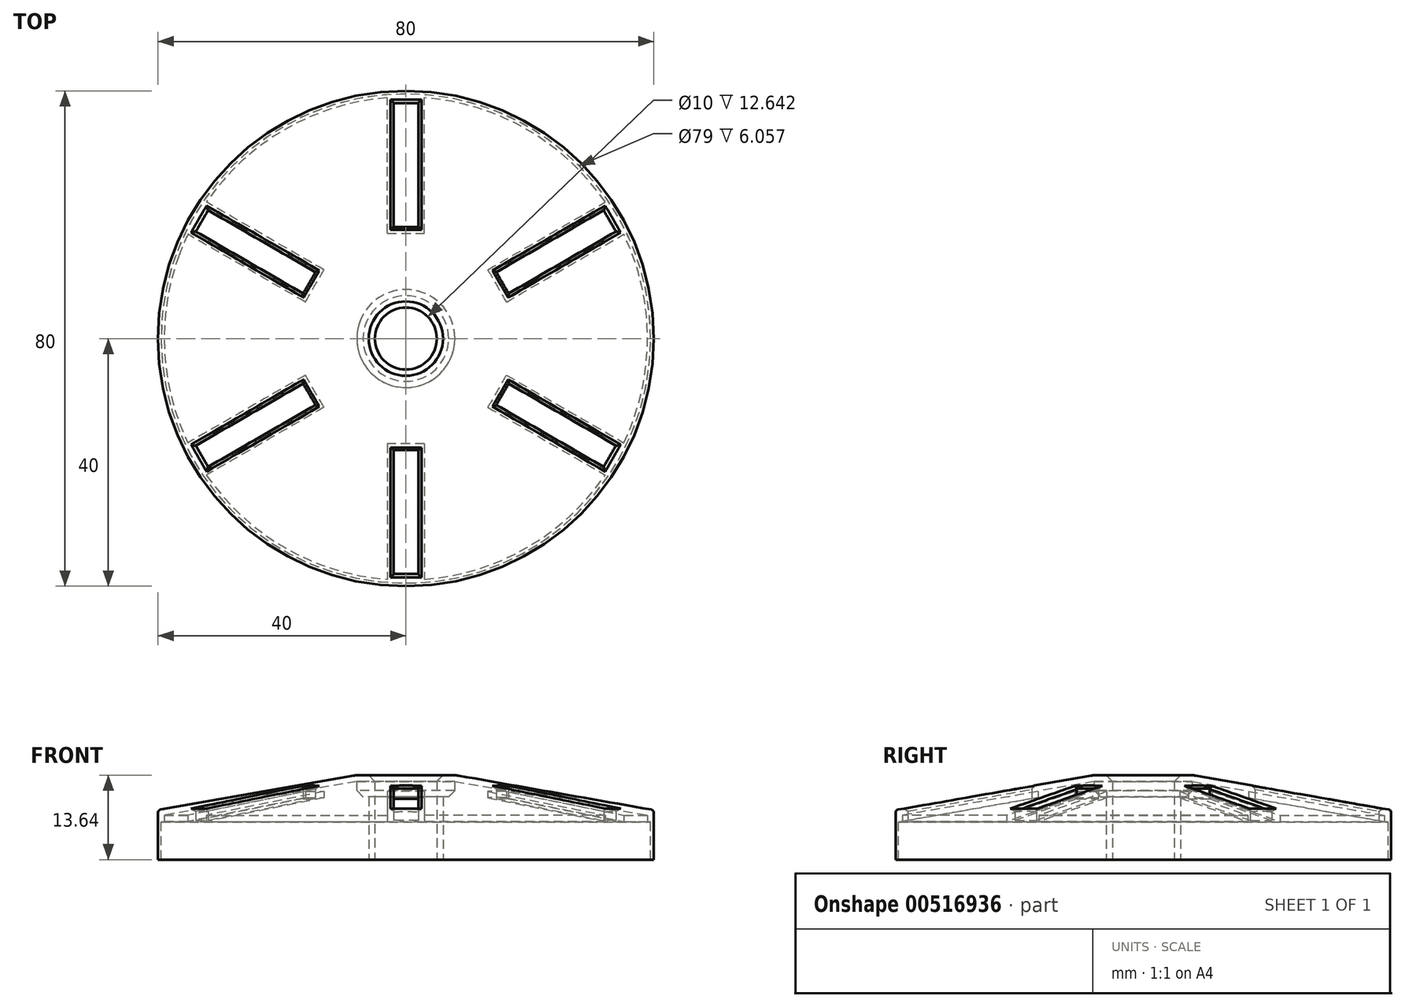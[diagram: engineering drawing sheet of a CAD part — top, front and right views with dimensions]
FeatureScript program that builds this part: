
annotation { "Feature Type Name" : "Feature", "Feature Type Description" : "" }
export const myFeature = defineFeature(function(context is Context, id is Id, definition is map)
    precondition{}
    {
        {
            var Q0;
            Q0=qCreatedBy(makeId("Front.planeOp"),FACE);
            var sketch = newSketch(context, id + "F0", { "sketchPlane" : qUnion([Q0])});
            skLineSegment(sketch, "E0", {"start": v(0, 0) * mm, "end": v(-40, 0) * mm});
            skLineSegment(sketch, "E1", {"start": v(-40, 0) * mm, "end": v(-40, 8) * mm});
            skLineSegment(sketch, "E2", {"start": v(-40, 8) * mm, "end": v(-8, 13.64) * mm});
            skLineSegment(sketch, "E3", {"start": v(-8, 13.64) * mm, "end": v(0, 13.64) * mm});
            skLineSegment(sketch, "E4", {"start": v(0, 0) * mm, "end": v(0, 13.64) * mm});
            skLineSegment(sketch, "E5.0", {"start": v(-39.5, 6.06) * mm, "end": v(-8, 11.61) * mm});
            skLineSegment(sketch, "E6.0", {"start": v(-39.5, 0) * mm, "end": v(-39.5, 6.06) * mm});
            skLineSegment(sketch, "E7", {"start": v(-8, 11.61) * mm, "end": v(-8, 0) * mm});
            skSolve(sketch);
        }
        {
            var Q0;
            Q0=makeQuery(id+"F0.imprint","IMPRINT",FACE,{"disambiguationData":[TD([[makeQuery(id+"F0.imprint","IMPRINT",EDGE,{"derivedFrom":sQuery(id+"F0.wireOp",EDGE,"E0")}),-1.0]])]});
            var Q1;
            Q1=makeQuery(id+"F0.imprint","IMPRINT",FACE,{"disambiguationData":[TD([[makeQuery(id+"F0.imprint","IMPRINT",EDGE,{"derivedFrom":sQuery(id+"F0.wireOp",EDGE,"E5.0")}),-1.0]])]});
            var Q2;
            Q2=sQuery(id+"F0.wireOp",EDGE,"E4");
            revolve(context, id + "F1", {"entities" : qUnion([Q0, Q1]), "axis" : qUnion([Q2]), "revolveType" : RevolveType.FULL});
        }
        {
            var Q0;
            Q0=qCreatedBy(makeId("Top.planeOp"),FACE);
            var sketch = newSketch(context, id + "F2", { "sketchPlane" : qUnion([Q0])});
            skCircle(sketch, "E8", {"center": v(0, 0) * mm, "radius": 5 * mm});
            skLineSegment(sketch, "E9.bottom", {"start": v(2, 38) * mm, "end": v(-2, 38) * mm});
            skLineSegment(sketch, "E9.top", {"start": v(2, 18) * mm, "end": v(-2, 18) * mm});
            skLineSegment(sketch, "E9.left", {"start": v(2, 38) * mm, "end": v(2, 18) * mm});
            skLineSegment(sketch, "E9.right", {"start": v(-2, 38) * mm, "end": v(-2, 18) * mm});
            skPoint(sketch, "E9.middle", {"position": v(0, 28) * mm});
            skLineSegment(sketch, "E10.1.0", {"start": v(-33.9, 17.27) * mm, "end": v(-16.59, 7.27) * mm});
            skLineSegment(sketch, "E10.1.1", {"start": v(-31.9, 20.73) * mm, "end": v(-33.9, 17.27) * mm});
            skLineSegment(sketch, "E10.1.2", {"start": v(-31.9, 20.73) * mm, "end": v(-14.59, 10.73) * mm});
            skLineSegment(sketch, "E10.1.3", {"start": v(-14.59, 10.73) * mm, "end": v(-16.59, 7.27) * mm});
            skLineSegment(sketch, "E10.2.0", {"start": v(-31.9, -20.73) * mm, "end": v(-14.59, -10.73) * mm});
            skLineSegment(sketch, "E10.2.1", {"start": v(-33.9, -17.27) * mm, "end": v(-31.9, -20.73) * mm});
            skLineSegment(sketch, "E10.2.2", {"start": v(-33.9, -17.27) * mm, "end": v(-16.59, -7.27) * mm});
            skLineSegment(sketch, "E10.2.3", {"start": v(-16.59, -7.27) * mm, "end": v(-14.59, -10.73) * mm});
            skLineSegment(sketch, "E11.2.3.0", {"start": v(2, -38) * mm, "end": v(2, -18) * mm});
            skLineSegment(sketch, "E11.3.3.0", {"start": v(-2, -38) * mm, "end": v(2, -38) * mm});
            skLineSegment(sketch, "E11.6.3.0", {"start": v(-2, -38) * mm, "end": v(-2, -18) * mm});
            skLineSegment(sketch, "E11.9.3.0", {"start": v(-2, -18) * mm, "end": v(2, -18) * mm});
            skLineSegment(sketch, "E11.2.4.0", {"start": v(33.9, -17.27) * mm, "end": v(16.59, -7.27) * mm});
            skLineSegment(sketch, "E11.3.4.0", {"start": v(31.9, -20.73) * mm, "end": v(33.9, -17.27) * mm});
            skLineSegment(sketch, "E11.6.4.0", {"start": v(31.9, -20.73) * mm, "end": v(14.59, -10.73) * mm});
            skLineSegment(sketch, "E11.9.4.0", {"start": v(14.59, -10.73) * mm, "end": v(16.59, -7.27) * mm});
            skLineSegment(sketch, "E12.2.5.0", {"start": v(31.9, 20.73) * mm, "end": v(14.59, 10.73) * mm});
            skLineSegment(sketch, "E12.3.5.0", {"start": v(33.9, 17.27) * mm, "end": v(31.9, 20.73) * mm});
            skLineSegment(sketch, "E12.6.5.0", {"start": v(33.9, 17.27) * mm, "end": v(16.59, 7.27) * mm});
            skLineSegment(sketch, "E12.9.5.0", {"start": v(16.59, 7.27) * mm, "end": v(14.59, 10.73) * mm});
            skSolve(sketch);
        }
        {
            var Q0;
            Q0=makeQuery(id+"F2.imprint","IMPRINT",FACE,{"disambiguationData":[TD([[makeQuery(id+"F2.imprint","IMPRINT",EDGE,{"derivedFrom":sQuery(id+"F2.wireOp",EDGE,"E10.1.0")}),1.0]])]});
            var Q1;
            Q1=makeQuery(id+"F2.imprint","IMPRINT",FACE,{"disambiguationData":[TD([[makeQuery(id+"F2.imprint","IMPRINT",EDGE,{"derivedFrom":sQuery(id+"F2.wireOp",EDGE,"E10.2.0")}),1.0]])]});
            var Q2;
            Q2=makeQuery(id+"F2.imprint","IMPRINT",FACE,{"disambiguationData":[TD([[makeQuery(id+"F2.imprint","IMPRINT",EDGE,{"derivedFrom":sQuery(id+"F2.wireOp",EDGE,"E8")}),1.0]])]});
            var Q3;
            Q3=makeQuery(id+"F2.imprint","IMPRINT",FACE,{"disambiguationData":[TD([[makeQuery(id+"F2.imprint","IMPRINT",EDGE,{"derivedFrom":sQuery(id+"F2.wireOp",EDGE,"E9.bottom")}),1.0]])]});
            var Q4;
            Q4=makeQuery(id+"F2.imprint","IMPRINT",FACE,{"disambiguationData":[TD([[makeQuery(id+"F2.imprint","IMPRINT",EDGE,{"derivedFrom":sQuery(id+"F2.wireOp",EDGE,"E11.2.3.0")}),1.0]])]});
            var Q5;
            Q5=makeQuery(id+"F2.imprint","IMPRINT",FACE,{"disambiguationData":[TD([[makeQuery(id+"F2.imprint","IMPRINT",EDGE,{"derivedFrom":sQuery(id+"F2.wireOp",EDGE,"E11.2.4.0")}),1.0]])]});
            var Q6;
            Q6=makeQuery(id+"F2.imprint","IMPRINT",FACE,{"disambiguationData":[TD([[makeQuery(id+"F2.imprint","IMPRINT",EDGE,{"derivedFrom":sQuery(id+"F2.wireOp",EDGE,"E12.2.5.0")}),1.0]])]});
            extrude(context, id + "F3", {"entities" : qUnion([Q0, Q1, Q2, Q3, Q4, Q5, Q6]), "operationType" : NewBodyOperationType.REMOVE, "endBound" : BoundingType.THROUGH_ALL, "depth" : 25 * mm, "offsetDistance" : 25 * mm});
        }
        {
            var Q0;
            Q0=makeQuery(id+"F1.opRevolve","SWEPT_FACE",FACE,{"disambiguationData":[OSD([sQuery(id+"F0.wireOp",EDGE,"E0")])]});
            shell(context, id + "F4", {"entities" : qUnion([Q0]), "thickness" : 1 * mm});
        }
        {
            var Q0;
            Q0=makeQuery(id+"F1.opRevolve","SWEPT_EDGE",EDGE,{"disambiguationData":[OSD([sQuery(id+"F0.wireOp",EDGE,"E2"),sQuery(id+"F0.wireOp",EDGE,"E3")])]});
            fillet(context, id + "F5", {"entities" : qUnion([Q0]), "radius" : 5 * mm, "tangentPropagation" : true, "allowEdgeOverflow" : false});
        }
        {
            var Q0;
            Q0=makeQuery(id+"F3.boolean.opBoolean","INTERSECT",EDGE,{"derivedFrom":[makeQuery(id+"F1.opRevolve","SWEPT_FACE",FACE,{"disambiguationData":[OSD([sQuery(id+"F0.wireOp",EDGE,"E3")])]}),makeQuery(id+"F3.opExtrude","SWEPT_FACE",FACE,{"disambiguationData":[OSD([sQuery(id+"F2.wireOp",EDGE,"E8")])]})]});
            chamfer(context, id + "F6", {"entities" : qUnion([Q0]), "width" : 1 * mm, "tangentPropagation" : true});
        }
        {
            var Q0;
            Q0=makeQuery(id+"F3.boolean.opBoolean","INTERSECT",EDGE,{"derivedFrom":[makeQuery(id+"F1.opRevolve","SWEPT_FACE",FACE,{"disambiguationData":[OSD([sQuery(id+"F0.wireOp",EDGE,"E2")])]}),makeQuery(id+"F3.opExtrude","SWEPT_FACE",FACE,{"disambiguationData":[OSD([sQuery(id+"F2.wireOp",EDGE,"E10.1.2")])]})]});
            var Q1;
            Q1=makeQuery(id+"F3.boolean.opBoolean","INTERSECT",EDGE,{"derivedFrom":[makeQuery(id+"F1.opRevolve","SWEPT_FACE",FACE,{"disambiguationData":[OSD([sQuery(id+"F0.wireOp",EDGE,"E2")])]}),makeQuery(id+"F3.opExtrude","SWEPT_FACE",FACE,{"disambiguationData":[OSD([sQuery(id+"F2.wireOp",EDGE,"E10.1.3")])]})]});
            var Q2;
            Q2=makeQuery(id+"F3.boolean.opBoolean","INTERSECT",EDGE,{"derivedFrom":[makeQuery(id+"F1.opRevolve","SWEPT_FACE",FACE,{"disambiguationData":[OSD([sQuery(id+"F0.wireOp",EDGE,"E2")])]}),makeQuery(id+"F3.opExtrude","SWEPT_FACE",FACE,{"disambiguationData":[OSD([sQuery(id+"F2.wireOp",EDGE,"E10.1.0")])]})]});
            var Q3;
            Q3=makeQuery(id+"F3.boolean.opBoolean","INTERSECT",EDGE,{"derivedFrom":[makeQuery(id+"F1.opRevolve","SWEPT_FACE",FACE,{"disambiguationData":[OSD([sQuery(id+"F0.wireOp",EDGE,"E2")])]}),makeQuery(id+"F3.opExtrude","SWEPT_FACE",FACE,{"disambiguationData":[OSD([sQuery(id+"F2.wireOp",EDGE,"E10.1.1")])]})]});
            var Q4;
            Q4=makeQuery(id+"F3.boolean.opBoolean","INTERSECT",EDGE,{"derivedFrom":[makeQuery(id+"F1.opRevolve","SWEPT_FACE",FACE,{"disambiguationData":[OSD([sQuery(id+"F0.wireOp",EDGE,"E2")])]}),makeQuery(id+"F3.opExtrude","SWEPT_FACE",FACE,{"disambiguationData":[OSD([sQuery(id+"F2.wireOp",EDGE,"E9.right")])]})]});
            var Q5;
            Q5=makeQuery(id+"F3.boolean.opBoolean","INTERSECT",EDGE,{"derivedFrom":[makeQuery(id+"F1.opRevolve","SWEPT_FACE",FACE,{"disambiguationData":[OSD([sQuery(id+"F0.wireOp",EDGE,"E2")])]}),makeQuery(id+"F3.opExtrude","SWEPT_FACE",FACE,{"disambiguationData":[OSD([sQuery(id+"F2.wireOp",EDGE,"E9.bottom")])]})]});
            var Q6;
            Q6=makeQuery(id+"F3.boolean.opBoolean","INTERSECT",EDGE,{"derivedFrom":[makeQuery(id+"F1.opRevolve","SWEPT_FACE",FACE,{"disambiguationData":[OSD([sQuery(id+"F0.wireOp",EDGE,"E2")])]}),makeQuery(id+"F3.opExtrude","SWEPT_FACE",FACE,{"disambiguationData":[OSD([sQuery(id+"F2.wireOp",EDGE,"E9.left")])]})]});
            var Q7;
            Q7=makeQuery(id+"F3.boolean.opBoolean","INTERSECT",EDGE,{"derivedFrom":[makeQuery(id+"F1.opRevolve","SWEPT_FACE",FACE,{"disambiguationData":[OSD([sQuery(id+"F0.wireOp",EDGE,"E2")])]}),makeQuery(id+"F3.opExtrude","SWEPT_FACE",FACE,{"disambiguationData":[OSD([sQuery(id+"F2.wireOp",EDGE,"E9.top")])]})]});
            var Q8;
            Q8=makeQuery(id+"F3.boolean.opBoolean","INTERSECT",EDGE,{"derivedFrom":[makeQuery(id+"F1.opRevolve","SWEPT_FACE",FACE,{"disambiguationData":[OSD([sQuery(id+"F0.wireOp",EDGE,"E2")])]}),makeQuery(id+"F3.opExtrude","SWEPT_FACE",FACE,{"disambiguationData":[OSD([sQuery(id+"F2.wireOp",EDGE,"E10.2.0")])]})]});
            var Q9;
            Q9=makeQuery(id+"F3.boolean.opBoolean","INTERSECT",EDGE,{"derivedFrom":[makeQuery(id+"F1.opRevolve","SWEPT_FACE",FACE,{"disambiguationData":[OSD([sQuery(id+"F0.wireOp",EDGE,"E2")])]}),makeQuery(id+"F3.opExtrude","SWEPT_FACE",FACE,{"disambiguationData":[OSD([sQuery(id+"F2.wireOp",EDGE,"E10.2.3")])]})]});
            var Q10;
            Q10=makeQuery(id+"F3.boolean.opBoolean","INTERSECT",EDGE,{"derivedFrom":[makeQuery(id+"F1.opRevolve","SWEPT_FACE",FACE,{"disambiguationData":[OSD([sQuery(id+"F0.wireOp",EDGE,"E2")])]}),makeQuery(id+"F3.opExtrude","SWEPT_FACE",FACE,{"disambiguationData":[OSD([sQuery(id+"F2.wireOp",EDGE,"E10.2.2")])]})]});
            var Q11;
            Q11=makeQuery(id+"F3.boolean.opBoolean","INTERSECT",EDGE,{"derivedFrom":[makeQuery(id+"F1.opRevolve","SWEPT_FACE",FACE,{"disambiguationData":[OSD([sQuery(id+"F0.wireOp",EDGE,"E2")])]}),makeQuery(id+"F3.opExtrude","SWEPT_FACE",FACE,{"disambiguationData":[OSD([sQuery(id+"F2.wireOp",EDGE,"E10.2.1")])]})]});
            var Q12;
            Q12=makeQuery(id+"F3.boolean.opBoolean","INTERSECT",EDGE,{"derivedFrom":[makeQuery(id+"F1.opRevolve","SWEPT_FACE",FACE,{"disambiguationData":[OSD([sQuery(id+"F0.wireOp",EDGE,"E2")])]}),makeQuery(id+"F3.opExtrude","SWEPT_FACE",FACE,{"disambiguationData":[OSD([sQuery(id+"F2.wireOp",EDGE,"E11.9.4.0")])]})]});
            var Q13;
            Q13=makeQuery(id+"F3.boolean.opBoolean","INTERSECT",EDGE,{"derivedFrom":[makeQuery(id+"F1.opRevolve","SWEPT_FACE",FACE,{"disambiguationData":[OSD([sQuery(id+"F0.wireOp",EDGE,"E2")])]}),makeQuery(id+"F3.opExtrude","SWEPT_FACE",FACE,{"disambiguationData":[OSD([sQuery(id+"F2.wireOp",EDGE,"E11.2.4.0")])]})]});
            var Q14;
            Q14=makeQuery(id+"F3.boolean.opBoolean","INTERSECT",EDGE,{"derivedFrom":[makeQuery(id+"F1.opRevolve","SWEPT_FACE",FACE,{"disambiguationData":[OSD([sQuery(id+"F0.wireOp",EDGE,"E2")])]}),makeQuery(id+"F3.opExtrude","SWEPT_FACE",FACE,{"disambiguationData":[OSD([sQuery(id+"F2.wireOp",EDGE,"E11.6.4.0")])]})]});
            var Q15;
            Q15=makeQuery(id+"F3.boolean.opBoolean","INTERSECT",EDGE,{"derivedFrom":[makeQuery(id+"F1.opRevolve","SWEPT_FACE",FACE,{"disambiguationData":[OSD([sQuery(id+"F0.wireOp",EDGE,"E2")])]}),makeQuery(id+"F3.opExtrude","SWEPT_FACE",FACE,{"disambiguationData":[OSD([sQuery(id+"F2.wireOp",EDGE,"E11.3.4.0")])]})]});
            var Q16;
            Q16=makeQuery(id+"F3.boolean.opBoolean","INTERSECT",EDGE,{"derivedFrom":[makeQuery(id+"F1.opRevolve","SWEPT_FACE",FACE,{"disambiguationData":[OSD([sQuery(id+"F0.wireOp",EDGE,"E2")])]}),makeQuery(id+"F3.opExtrude","SWEPT_FACE",FACE,{"disambiguationData":[OSD([sQuery(id+"F2.wireOp",EDGE,"E11.9.3.0")])]})]});
            var Q17;
            Q17=makeQuery(id+"F3.boolean.opBoolean","INTERSECT",EDGE,{"derivedFrom":[makeQuery(id+"F1.opRevolve","SWEPT_FACE",FACE,{"disambiguationData":[OSD([sQuery(id+"F0.wireOp",EDGE,"E2")])]}),makeQuery(id+"F3.opExtrude","SWEPT_FACE",FACE,{"disambiguationData":[OSD([sQuery(id+"F2.wireOp",EDGE,"E11.6.3.0")])]})]});
            var Q18;
            Q18=makeQuery(id+"F3.boolean.opBoolean","INTERSECT",EDGE,{"derivedFrom":[makeQuery(id+"F1.opRevolve","SWEPT_FACE",FACE,{"disambiguationData":[OSD([sQuery(id+"F0.wireOp",EDGE,"E2")])]}),makeQuery(id+"F3.opExtrude","SWEPT_FACE",FACE,{"disambiguationData":[OSD([sQuery(id+"F2.wireOp",EDGE,"E11.2.3.0")])]})]});
            var Q19;
            Q19=makeQuery(id+"F3.boolean.opBoolean","INTERSECT",EDGE,{"derivedFrom":[makeQuery(id+"F1.opRevolve","SWEPT_FACE",FACE,{"disambiguationData":[OSD([sQuery(id+"F0.wireOp",EDGE,"E2")])]}),makeQuery(id+"F3.opExtrude","SWEPT_FACE",FACE,{"disambiguationData":[OSD([sQuery(id+"F2.wireOp",EDGE,"E11.3.3.0")])]})]});
            var Q20;
            Q20=makeQuery(id+"F3.boolean.opBoolean","INTERSECT",EDGE,{"derivedFrom":[makeQuery(id+"F1.opRevolve","SWEPT_FACE",FACE,{"disambiguationData":[OSD([sQuery(id+"F0.wireOp",EDGE,"E2")])]}),makeQuery(id+"F3.opExtrude","SWEPT_FACE",FACE,{"disambiguationData":[OSD([sQuery(id+"F2.wireOp",EDGE,"E12.3.5.0")])]})]});
            var Q21;
            Q21=makeQuery(id+"F3.boolean.opBoolean","INTERSECT",EDGE,{"derivedFrom":[makeQuery(id+"F1.opRevolve","SWEPT_FACE",FACE,{"disambiguationData":[OSD([sQuery(id+"F0.wireOp",EDGE,"E2")])]}),makeQuery(id+"F3.opExtrude","SWEPT_FACE",FACE,{"disambiguationData":[OSD([sQuery(id+"F2.wireOp",EDGE,"E12.6.5.0")])]})]});
            var Q22;
            Q22=makeQuery(id+"F3.boolean.opBoolean","INTERSECT",EDGE,{"derivedFrom":[makeQuery(id+"F1.opRevolve","SWEPT_FACE",FACE,{"disambiguationData":[OSD([sQuery(id+"F0.wireOp",EDGE,"E2")])]}),makeQuery(id+"F3.opExtrude","SWEPT_FACE",FACE,{"disambiguationData":[OSD([sQuery(id+"F2.wireOp",EDGE,"E12.9.5.0")])]})]});
            var Q23;
            Q23=makeQuery(id+"F3.boolean.opBoolean","INTERSECT",EDGE,{"derivedFrom":[makeQuery(id+"F1.opRevolve","SWEPT_FACE",FACE,{"disambiguationData":[OSD([sQuery(id+"F0.wireOp",EDGE,"E2")])]}),makeQuery(id+"F3.opExtrude","SWEPT_FACE",FACE,{"disambiguationData":[OSD([sQuery(id+"F2.wireOp",EDGE,"E12.2.5.0")])]})]});
            chamfer(context, id + "F7", {"entities" : qUnion([Q0, Q1, Q2, Q3, Q4, Q5, Q6, Q7, Q8, Q9, Q10, Q11, Q12, Q13, Q14, Q15, Q16, Q17, Q18, Q19, Q20, Q21, Q22, Q23]), "width" : 0.5 * mm, "tangentPropagation" : true});
        }
        {
            var Q0;
            Q0=makeQuery(id+"F1.opRevolve","SWEPT_EDGE",EDGE,{"disambiguationData":[OSD([sQuery(id+"F0.wireOp",EDGE,"E1"),sQuery(id+"F0.wireOp",EDGE,"E2")])]});
            fillet(context, id + "F8", {"entities" : qUnion([Q0]), "radius" : .5 * mm, "tangentPropagation" : true, "allowEdgeOverflow" : false});
        }
        {
            var Q0;
            Q0=makeQuery(id+"F0.imprint","IMPRINT",FACE,{"disambiguationData":[TD([[makeQuery(id+"F0.imprint","IMPRINT",EDGE,{"derivedFrom":sQuery(id+"F0.wireOp",EDGE,"E5.0")}),-1.0]])]});
            var Q1;
            Q1=sQuery(id+"F0.wireOp",EDGE,"E4");
            revolve(context, id + "F9", {"operationType" : NewBodyOperationType.REMOVE, "entities" : qUnion([Q0]), "axis" : qUnion([Q1]), "revolveType" : RevolveType.FULL, "oppositeDirection" : true});
        }
        {
            var Q0;
            Q0=makeQuery(id+"F4.opShell","OFFSET_FACE",FACE,{"disambiguationData":[OSD([sQuery(id+"F0.wireOp",EDGE,"E3")])]});
            extrude(context, id + "F10", {"entities" : qUnion([Q0]), "operationType" : NewBodyOperationType.ADD, "depth" : 2.5 * mm, "offsetDistance" : 25 * mm});
        }
        {
            var Q0;
            Q0=makeQuery(id+"F10.opExtrude","CAP_EDGE",EDGE,{"disambiguationData":[OSD([sQuery(id+"F0.wireOp",EDGE,"E2"),sQuery(id+"F0.wireOp",EDGE,"E3")])],"isStart":false});
            chamfer(context, id + "F11", {"entities" : qUnion([Q0]), "width" : 1 * mm, "tangentPropagation" : true});
        }
    });
